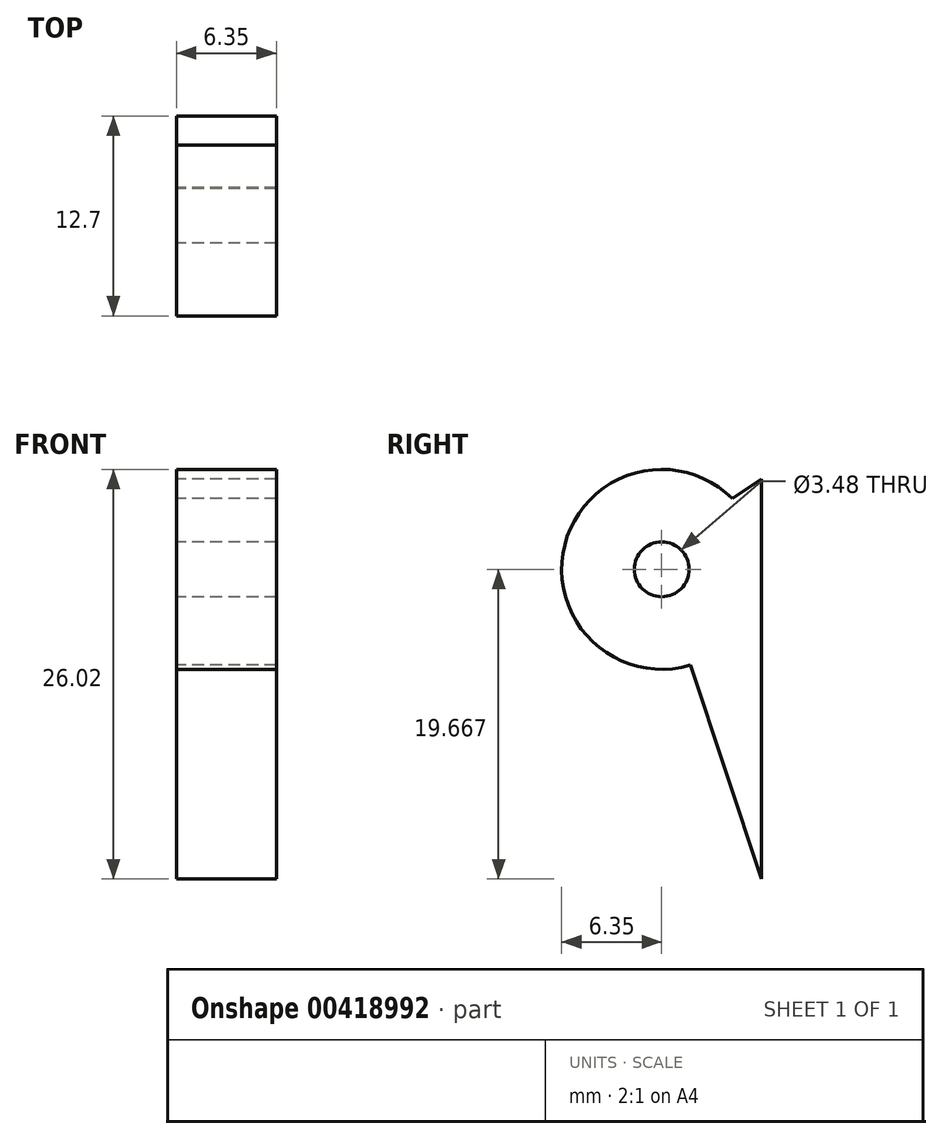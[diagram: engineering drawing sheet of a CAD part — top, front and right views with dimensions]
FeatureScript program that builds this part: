
annotation { "Feature Type Name" : "Feature", "Feature Type Description" : "" }
export const myFeature = defineFeature(function(context is Context, id is Id, definition is map)
    precondition{}
    {
        {
            var Q0;
            Q0=qCreatedBy(makeId("Right.planeOp"),FACE);
            var sketch = newSketch(context, id + "F0", { "sketchPlane" : qUnion([Q0])});
            skLineSegment(sketch, "E0", {"start": v(-44.45, 18.73) * mm, "end": v(-44.45, -6.67) * mm});
            skCircle(sketch, "E1", {"center": v(-50.8, 13) * mm, "radius": 1.74 * mm});
            skLineSegment(sketch, "E2", {"start": v(-44.45, 18.73) * mm, "end": v(-50.5, 14.71) * mm});
            skLineSegment(sketch, "E3", {"start": v(-44.45, -6.67) * mm, "end": v(-50.45, 11.3) * mm});
            skCircle(sketch, "E4", {"center": v(-50.8, 13) * mm, "radius": 6.35 * mm});
            skSolve(sketch);
        }
        {
            var Q0;
            {var subQ0=sQuery(id+"F0.wireOp",EDGE,"E0");Q0=makeQuery(id+"F0.imprint","IMPRINT",FACE,{"disambiguationData":[TD([[makeQuery(id+"F0.imprint","IMPRINT",EDGE,{"derivedFrom":subQ0}),1.0]])]});}
            var Q1;
            {var subQ0=sQuery(id+"F0.wireOp",EDGE,"E2");var subQ1=sQuery(id+"F0.wireOp",EDGE,"E1");var subQ2=makeQuery(id+"F0.imprint","INTERSECT",VERTEX,{"derivedFrom":[subQ1,subQ0]});Q1=makeQuery(id+"F0.imprint","IMPRINT",FACE,{"disambiguationData":[TD([[makeQuery(id+"F0.imprint","IMPRINT",EDGE,{"disambiguationData":[TD([[subQ2,-1.0]])],"derivedFrom":subQ1}),-1.0]])]});}
            var Q2;
            {var subQ0=sQuery(id+"F0.wireOp",EDGE,"E2");var subQ1=sQuery(id+"F0.wireOp",EDGE,"E1");var subQ2=makeQuery(id+"F0.imprint","INTERSECT",VERTEX,{"derivedFrom":[subQ1,subQ0]});Q2=makeQuery(id+"F0.imprint","IMPRINT",FACE,{"disambiguationData":[TD([[makeQuery(id+"F0.imprint","IMPRINT",EDGE,{"disambiguationData":[TD([[subQ2,1.0]])],"derivedFrom":subQ1}),-1.0]])]});}
            var Q3;
            {var subQ0=sQuery(id+"F0.wireOp",EDGE,"E3");var subQ1=sQuery(id+"F0.wireOp",EDGE,"E0");var subQ2=makeQuery(id+"F0.imprint","INTERSECT",VERTEX,{"derivedFrom":[subQ1,subQ0]});Q3=makeQuery(id+"F0.imprint","IMPRINT",FACE,{"disambiguationData":[TD([[makeQuery(id+"F0.imprint","IMPRINT",EDGE,{"disambiguationData":[TD([[subQ2,1.0]])],"derivedFrom":subQ1}),-1.0]])]});}
            var Q4;
            {var subQ0=sQuery(id+"F0.wireOp",EDGE,"E2");var subQ1=sQuery(id+"F0.wireOp",EDGE,"E0");var subQ2=makeQuery(id+"F0.imprint","INTERSECT",VERTEX,{"derivedFrom":[subQ1,subQ0]});Q4=makeQuery(id+"F0.imprint","IMPRINT",FACE,{"disambiguationData":[TD([[makeQuery(id+"F0.imprint","IMPRINT",EDGE,{"disambiguationData":[TD([[subQ2,-1.0]])],"derivedFrom":subQ1}),-1.0]])]});}
            extrude(context, id + "F1", {"entities" : qUnion([Q0, Q1, Q2, Q3, Q4]), "depth" : 6.35 * mm});
        }
    });
